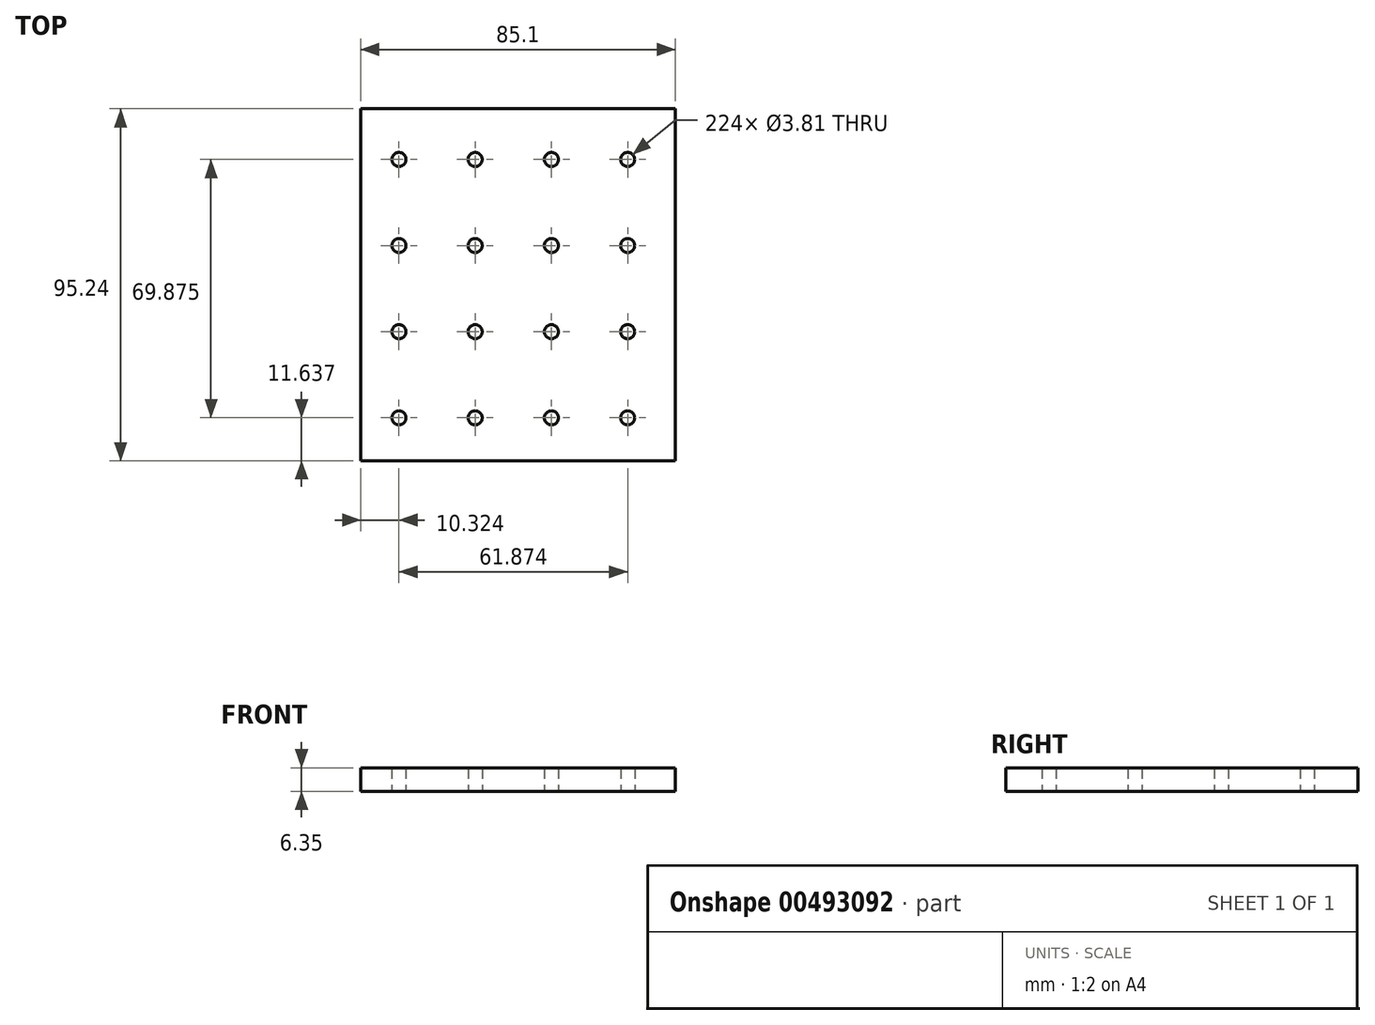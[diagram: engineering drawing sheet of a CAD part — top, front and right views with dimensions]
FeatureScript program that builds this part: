
annotation { "Feature Type Name" : "Feature", "Feature Type Description" : "" }
export const myFeature = defineFeature(function(context is Context, id is Id, definition is map)
    precondition{}
    {
        {
            var Q0;
            Q0=qCreatedBy(makeId("Top.planeOp"),FACE);
            var sketch = newSketch(context, id + "F0", { "sketchPlane" : qUnion([Q0])});
            skLineSegment(sketch, "E0.bottom", {"start": v(-42.55, 47.63) * mm, "end": v(42.55, 47.63) * mm});
            skLineSegment(sketch, "E0.top", {"start": v(-42.55, -47.63) * mm, "end": v(42.55, -47.63) * mm});
            skLineSegment(sketch, "E0.left", {"start": v(-42.55, 47.63) * mm, "end": v(-42.55, -47.63) * mm});
            skLineSegment(sketch, "E0.right", {"start": v(42.55, 47.63) * mm, "end": v(42.55, -47.63) * mm});
            skPoint(sketch, "E0.middle", {"position": v(0, 0) * mm});
            skSolve(sketch);
        }
        {
            var Q0;
            Q0=qSketchRegion(id+"F0",true);
            extrude(context, id + "F1", {"entities" : qUnion([Q0]), "depth" : 6.35 * mm});
        }
        {
            var Q0;
            Q0=qCreatedBy(makeId("Top.planeOp"),FACE);
            var sketch = newSketch(context, id + "F2", { "sketchPlane" : qUnion([Q0])});
            skCircle(sketch, "E1", {"center": v(-32.23, -35.98) * mm, "radius": 1.9 * mm});
            skCircle(sketch, "E2.0.1.0", {"center": v(-32.23, -12.7) * mm, "radius": 1.9 * mm});
            skCircle(sketch, "E2.0.2.0", {"center": v(-32.23, 10.6) * mm, "radius": 1.9 * mm});
            skCircle(sketch, "E2.0.3.0", {"center": v(-32.23, 33.9) * mm, "radius": 1.9 * mm});
            skCircle(sketch, "E2.0.4.0", {"center": v(-32.23, 57.18) * mm, "radius": 1.9 * mm});
            skCircle(sketch, "E2.0.5.0", {"center": v(-32.23, 80.48) * mm, "radius": 1.9 * mm});
            skCircle(sketch, "E2.1.0.0", {"center": v(-11.6, -35.98) * mm, "radius": 1.9 * mm});
            skCircle(sketch, "E2.1.1.0", {"center": v(-11.6, -12.7) * mm, "radius": 1.9 * mm});
            skCircle(sketch, "E2.1.2.0", {"center": v(-11.6, 10.6) * mm, "radius": 1.9 * mm});
            skCircle(sketch, "E2.1.3.0", {"center": v(-11.6, 33.9) * mm, "radius": 1.9 * mm});
            skCircle(sketch, "E2.1.4.0", {"center": v(-11.6, 57.18) * mm, "radius": 1.9 * mm});
            skCircle(sketch, "E2.1.5.0", {"center": v(-11.6, 80.48) * mm, "radius": 1.9 * mm});
            skCircle(sketch, "E2.2.0.0", {"center": v(9.02, -35.98) * mm, "radius": 1.9 * mm});
            skCircle(sketch, "E2.2.1.0", {"center": v(9.02, -12.7) * mm, "radius": 1.9 * mm});
            skCircle(sketch, "E2.2.2.0", {"center": v(9.02, 10.6) * mm, "radius": 1.9 * mm});
            skCircle(sketch, "E2.2.3.0", {"center": v(9.02, 33.9) * mm, "radius": 1.9 * mm});
            skCircle(sketch, "E2.2.4.0", {"center": v(9.02, 57.18) * mm, "radius": 1.9 * mm});
            skCircle(sketch, "E2.2.5.0", {"center": v(9.02, 80.48) * mm, "radius": 1.9 * mm});
            skCircle(sketch, "E2.3.0.0", {"center": v(29.65, -35.98) * mm, "radius": 1.9 * mm});
            skCircle(sketch, "E2.3.1.0", {"center": v(29.65, -12.7) * mm, "radius": 1.9 * mm});
            skCircle(sketch, "E2.3.2.0", {"center": v(29.65, 10.6) * mm, "radius": 1.9 * mm});
            skCircle(sketch, "E2.3.3.0", {"center": v(29.65, 33.9) * mm, "radius": 1.9 * mm});
            skCircle(sketch, "E2.3.4.0", {"center": v(29.65, 57.18) * mm, "radius": 1.9 * mm});
            skCircle(sketch, "E2.3.5.0", {"center": v(29.65, 80.48) * mm, "radius": 1.9 * mm});
            skLineSegment(sketch, "E2.direction1", {"start": v(-32.23, -35.98) * mm, "end": v(-11.6, -35.98) * mm, "construction": true});
            skLineSegment(sketch, "E2.direction2", {"start": v(-32.23, -35.98) * mm, "end": v(-32.23, -12.7) * mm, "construction": true});
            skSolve(sketch);
        }
        {
            var Q0;
            Q0=qSketchRegion(id+"F2",true);
            extrude(context, id + "F3", {"entities" : qUnion([Q0]), "operationType" : NewBodyOperationType.REMOVE, "endBound" : BoundingType.THROUGH_ALL, "depth" : 25.4 * mm});
        }
    });
